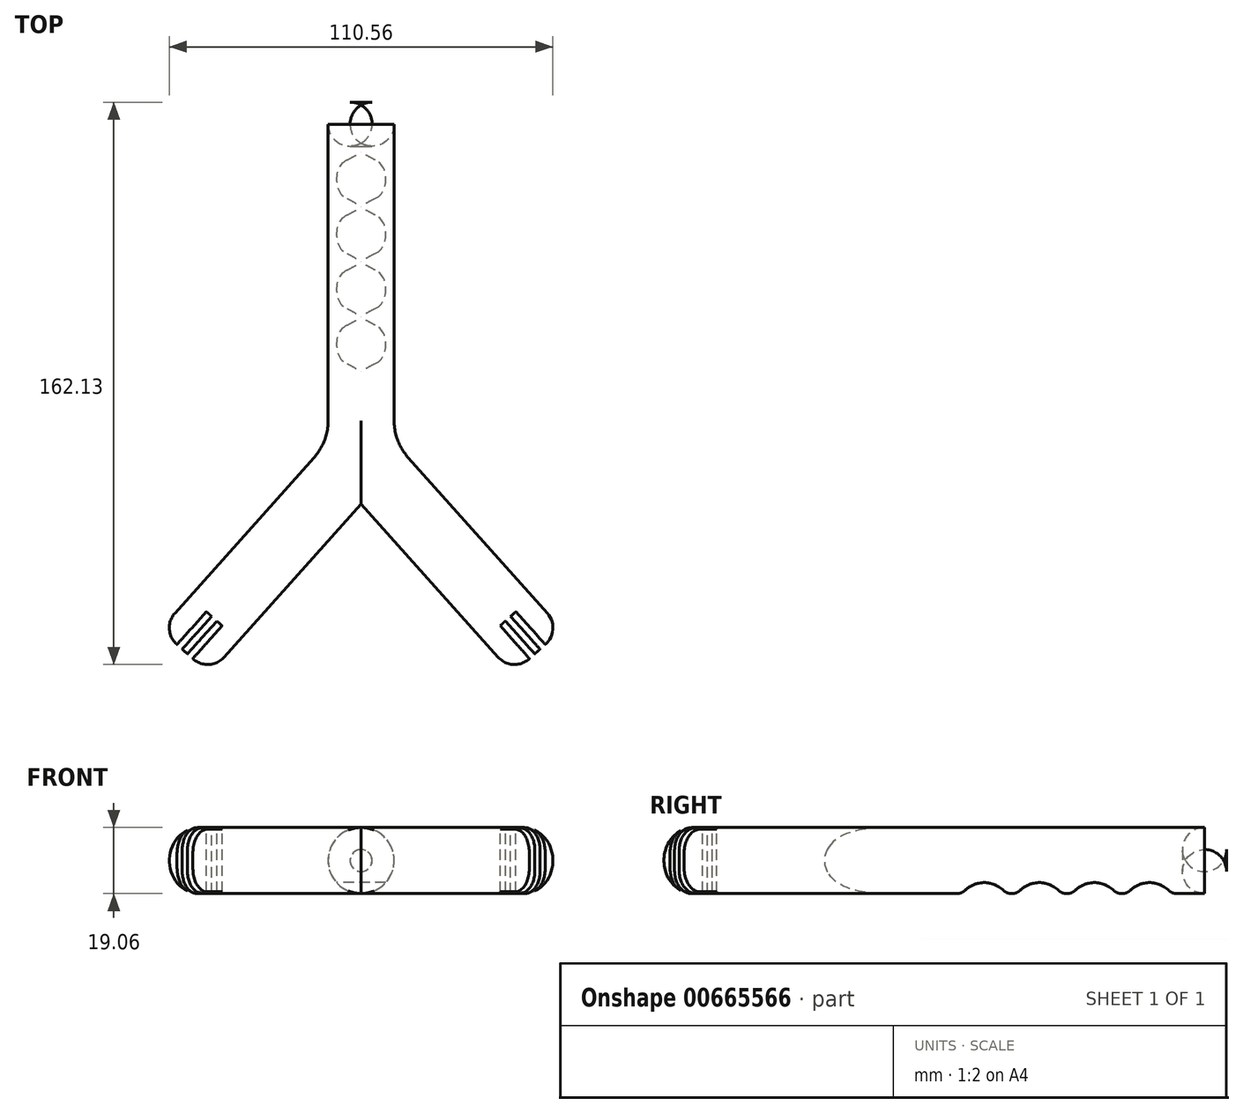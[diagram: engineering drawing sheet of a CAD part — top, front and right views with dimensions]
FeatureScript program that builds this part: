
annotation { "Feature Type Name" : "Feature", "Feature Type Description" : "" }
export const myFeature = defineFeature(function(context is Context, id is Id, definition is map)
    precondition{}
    {
        {
            var Q0;
            Q0=qCreatedBy(makeId("Front.planeOp"),FACE);
            var sketch = newSketch(context, id + "F0", { "sketchPlane" : qUnion([Q0])});
            skCircle(sketch, "E0", {"center": v(0, 0) * mm, "radius": 9.53 * mm});
            skSolve(sketch);
        }
        {
            var Q0;
            Q0=qCreatedBy(makeId("Top.planeOp"),FACE);
            var sketch = newSketch(context, id + "F1", { "sketchPlane" : qUnion([Q0])});
            skLineSegment(sketch, "E1", {"start": v(6.47, -108.83) * mm, "end": v(50.8, -158.4) * mm});
            skLineSegment(sketch, "E2", {"start": v(0, -91.9) * mm, "end": v(0, 0) * mm});
            skPoint(sketch, "E3.visualSharp", {"position": v(0, -101.6) * mm});
            skArc(sketch, "E3.filletArc", {"start": v(0, -91.9) * mm, "mid": v(1.67, -100.96) * mm, "end": v(6.47, -108.83) * mm});
            skSolve(sketch);
        }
        {
            var Q0;
            Q0=makeQuery(id+"F0.imprint","IMPRINT",FACE,{"disambiguationData":[TD([[makeQuery(id+"F0.imprint","IMPRINT",EDGE,{"derivedFrom":sQuery(id+"F0.wireOp",EDGE,"E0")}),1.0]])]});
            var Q1;
            Q1=sQuery(id+"F1.wireOp",EDGE,"E2");
            var Q2;
            Q2=sQuery(id+"F1.wireOp",EDGE,"E1");
            var Q3;
            Q3=sQuery(id+"F1.wireOp",EDGE,"3JrWUsI6-woq9-sjH6-vDIZ-4JQYBJ9BbOre");
            var Q4;
            Q4=sQuery(id+"F1.wireOp",EDGE,"61547c2f-0ffb-42c4-a759-9a06780f6b13.filletArc");
            var Q5;
            Q5=sQuery(id+"F1.wireOp",EDGE,"E3.filletArc");
            sweep(context, id + "F2", {"profiles" : qUnion([Q0]), "path" : qUnion([Q1, Q2, Q3, Q4, Q5])});
        }
        {
            var Q0;
            Q0=qCreatedBy(makeId("Top.planeOp"),FACE);
            var sketch = newSketch(context, id + "F3", { "sketchPlane" : qUnion([Q0])});
            skLineSegment(sketch, "E4", {"start": v(0, 0) * mm, "end": v(0, -91.9) * mm});
            skLineSegment(sketch, "E5", {"start": v(-6.47, -108.83) * mm, "end": v(-50.8, -158.4) * mm});
            skPoint(sketch, "E6.visualSharp", {"position": v(0, -101.6) * mm});
            skArc(sketch, "E6.filletArc", {"start": v(-6.47, -108.83) * mm, "mid": v(-1.67, -100.96) * mm, "end": v(0, -91.9) * mm});
            skSolve(sketch);
        }
        {
            var Q0;
            Q0=makeQuery(id+"F2.opSweep","CAP_FACE",FACE,{"disambiguationData":[OSD([sQuery(id+"F0.wireOp",EDGE,"E0"),sQuery(id+"F1.wireOp",VERTEX,"E2.end")])],"isStart":true});
            var Q1;
            Q1=sQuery(id+"F3.wireOp",EDGE,"E4");
            var Q2;
            Q2=sQuery(id+"F3.wireOp",EDGE,"E6.filletArc");
            var Q3;
            Q3=sQuery(id+"F3.wireOp",EDGE,"E5");
            sweep(context, id + "F4", {"operationType" : NewBodyOperationType.ADD, "profiles" : qUnion([Q0]), "path" : qUnion([Q1, Q2, Q3])});
        }
        {
            var Q0;
            Q0=makeQuery(id+"F2.opSweep","CAP_EDGE",EDGE,{"disambiguationData":[OSD([sQuery(id+"F0.wireOp",EDGE,"E0"),sQuery(id+"F1.wireOp",VERTEX,"E1.end")])],"isStart":false});
            var Q1;
            Q1=makeQuery(id+"F4.opSweep","CAP_EDGE",EDGE,{"disambiguationData":[OSD([sQuery(id+"F0.wireOp",EDGE,"E0"),sQuery(id+"F1.wireOp",VERTEX,"E2.end"),sQuery(id+"F3.wireOp",VERTEX,"E5.end")])],"isStart":false});
            var Q2;
            Q2=makeQuery(id+"F2.opSweep","CAP_EDGE",EDGE,{"disambiguationData":[OSD([sQuery(id+"F0.wireOp",EDGE,"E0"),sQuery(id+"F1.wireOp",VERTEX,"E2.end")])],"isStart":true});
            fillet(context, id + "F5", {"entities" : qUnion([Q0, Q1, Q2]), "radius" : 6.35 * mm, "tangentPropagation" : true, "allowEdgeOverflow" : false});
        }
        {
            var Q0;
            Q0=qCreatedBy(makeId("Top.planeOp"),FACE);
            var sketch = newSketch(context, id + "F6", { "sketchPlane" : qUnion([Q0])});
            skLineSegment(sketch, "E7", {"start": v(48.53, -160.43) * mm, "end": v(40.06, -150.96) * mm});
            skLineSegment(sketch, "E8", {"start": v(40.06, -150.96) * mm, "end": v(41.58, -149.6) * mm});
            skLineSegment(sketch, "E9", {"start": v(41.58, -149.6) * mm, "end": v(50.04, -159.07) * mm});
            skLineSegment(sketch, "E10", {"start": v(50.04, -159.07) * mm, "end": v(48.53, -160.43) * mm});
            skLineSegment(sketch, "E11", {"start": v(50.8, -158.4) * mm, "end": v(45.21, -152.15) * mm, "construction": true});
            skLineSegment(sketch, "E12.MirrorCS", {"start": v(44.6, -146.9) * mm, "end": v(43.1, -148.25) * mm});
            skLineSegment(sketch, "E13.MirrorCS", {"start": v(53.07, -156.36) * mm, "end": v(44.6, -146.9) * mm});
            skLineSegment(sketch, "E14.MirrorCS", {"start": v(51.56, -157.72) * mm, "end": v(53.07, -156.36) * mm});
            skLineSegment(sketch, "E15.MirrorCS", {"start": v(43.1, -148.25) * mm, "end": v(51.56, -157.72) * mm});
            skLineSegment(sketch, "E16", {"start": v(0, 0) * mm, "end": v(0, -157.78) * mm, "construction": true});
            skLineSegment(sketch, "E17.MirrorCS", {"start": v(-50.04, -159.07) * mm, "end": v(-48.53, -160.43) * mm});
            skLineSegment(sketch, "E18.MirrorCS", {"start": v(-51.56, -157.72) * mm, "end": v(-53.07, -156.36) * mm});
            skLineSegment(sketch, "E19.MirrorCS", {"start": v(-40.06, -150.96) * mm, "end": v(-41.58, -149.6) * mm});
            skLineSegment(sketch, "E20.MirrorCS", {"start": v(-44.6, -146.9) * mm, "end": v(-43.1, -148.25) * mm});
            skLineSegment(sketch, "E21.MirrorCS", {"start": v(-41.58, -149.6) * mm, "end": v(-50.04, -159.07) * mm});
            skLineSegment(sketch, "E22.MirrorCS", {"start": v(-50.8, -158.4) * mm, "end": v(-45.21, -152.15) * mm, "construction": true});
            skLineSegment(sketch, "E23.MirrorCS", {"start": v(-48.53, -160.43) * mm, "end": v(-40.06, -150.96) * mm});
            skLineSegment(sketch, "E24.MirrorCS", {"start": v(-43.1, -148.25) * mm, "end": v(-51.56, -157.72) * mm});
            skLineSegment(sketch, "E25.MirrorCS", {"start": v(-53.07, -156.36) * mm, "end": v(-44.6, -146.9) * mm});
            skSolve(sketch);
        }
        {
            var Q0;
            Q0 = qSketchRegion(id + "F6", true);
            extrude(context, id + "F7", {"entities" : qUnion([Q0]), "operationType" : NewBodyOperationType.REMOVE, "endBound" : BoundingType.THROUGH_ALL, "oppositeDirection" : true, "depth" : 25.4 * mm, "offsetDistance" : 25.4 * mm, "hasSecondDirection" : true, "secondDirectionBound" : SecondDirectionBoundingType.THROUGH_ALL, "secondDirectionOppositeDirection" : false, "secondDirectionDepth" : 25.4 * mm});
        }
        {
            var Q0;
            Q0=qCreatedBy(makeId("Right.planeOp"),FACE);
            var sketch = newSketch(context, id + "F8", { "sketchPlane" : qUnion([Q0])});
            skLineSegment(sketch, "E26", {"start": v(-6.35, -9.52) * mm, "end": v(-14.45, -9.52) * mm, "construction": true});
            skLineSegment(sketch, "E27.0", {"start": v(-6.35, -9.53) * mm, "end": v(-6.35, 9.53) * mm, "construction": true});
            skArc(sketch, "E28", {"start": v(-16.67, -8.62) * mm, "mid": v(-22.22, -6.35) * mm, "end": v(-27.78, -8.62) * mm});
            skArc(sketch, "E29", {"start": v(-32.54, -8.62) * mm, "mid": v(-38.1, -6.35) * mm, "end": v(-43.66, -8.62) * mm});
            skArc(sketch, "E30", {"start": v(-48.42, -8.62) * mm, "mid": v(-53.98, -6.35) * mm, "end": v(-59.53, -8.62) * mm});
            skArc(sketch, "E31", {"start": v(-64.3, -8.62) * mm, "mid": v(-69.85, -6.35) * mm, "end": v(-75.4, -8.62) * mm});
            skLineSegment(sketch, "E32", {"start": v(-30, -9.52) * mm, "end": v(-30.32, -9.52) * mm});
            skLineSegment(sketch, "E33", {"start": v(-46.2, -9.52) * mm, "end": v(-45.88, -9.52) * mm});
            skLineSegment(sketch, "E34", {"start": v(-62.07, -9.52) * mm, "end": v(-61.75, -9.52) * mm});
            skLineSegment(sketch, "E35", {"start": v(-15.88, -9.52) * mm, "end": v(-28.58, -9.52) * mm, "construction": true});
            skLineSegment(sketch, "E36", {"start": v(-31.75, -9.52) * mm, "end": v(-44.45, -9.52) * mm, "construction": true});
            skLineSegment(sketch, "E37", {"start": v(-47.62, -9.52) * mm, "end": v(-60.33, -9.52) * mm, "construction": true});
            skLineSegment(sketch, "E38", {"start": v(-63.5, -9.52) * mm, "end": v(-76.2, -9.52) * mm, "construction": true});
            skLineSegment(sketch, "E39", {"start": v(-46.04, -9.52) * mm, "end": v(-46.04, -8.23) * mm, "construction": true});
            skLineSegment(sketch, "E40", {"start": v(-69.85, -6.35) * mm, "end": v(-22.23, -6.35) * mm, "construction": true});
            skPoint(sketch, "E41.newPointA", {"position": v(-15.88, -9.53) * mm});
            skPoint(sketch, "E41.newPointB", {"position": v(-85.72, -9.52) * mm});
            skArc(sketch, "E41.filletArc", {"start": v(-16.67, -8.62) * mm, "mid": v(-15.65, -9.29) * mm, "end": v(-14.45, -9.52) * mm});
            skPoint(sketch, "E42.visualSharp", {"position": v(-28.58, -9.53) * mm});
            skArc(sketch, "E42.filletArc", {"start": v(-30, -9.52) * mm, "mid": v(-28.8, -9.29) * mm, "end": v(-27.78, -8.62) * mm});
            skPoint(sketch, "E43.visualSharp", {"position": v(-31.75, -9.52) * mm});
            skArc(sketch, "E43.filletArc", {"start": v(-32.54, -8.62) * mm, "mid": v(-31.52, -9.29) * mm, "end": v(-30.32, -9.52) * mm});
            skPoint(sketch, "E44.visualSharp", {"position": v(-44.45, -9.52) * mm});
            skArc(sketch, "E44.filletArc", {"start": v(-45.88, -9.52) * mm, "mid": v(-44.68, -9.29) * mm, "end": v(-43.66, -8.62) * mm});
            skPoint(sketch, "E45.visualSharp", {"position": v(-47.62, -9.52) * mm});
            skArc(sketch, "E45.filletArc", {"start": v(-48.42, -8.62) * mm, "mid": v(-47.4, -9.29) * mm, "end": v(-46.2, -9.52) * mm});
            skPoint(sketch, "E46.visualSharp", {"position": v(-60.33, -9.52) * mm});
            skArc(sketch, "E46.filletArc", {"start": v(-61.75, -9.52) * mm, "mid": v(-60.55, -9.29) * mm, "end": v(-59.53, -8.62) * mm});
            skPoint(sketch, "E47.visualSharp", {"position": v(-63.5, -9.52) * mm});
            skArc(sketch, "E47.filletArc", {"start": v(-64.3, -8.62) * mm, "mid": v(-63.27, -9.29) * mm, "end": v(-62.07, -9.52) * mm});
            skLineSegment(sketch, "E48", {"start": v(-77.63, -9.53) * mm, "end": v(-78.14, -9.53) * mm, "construction": true});
            skPoint(sketch, "E49.visualSharp", {"position": v(-76.2, -9.53) * mm});
            skArc(sketch, "E49.filletArc", {"start": v(-77.63, -9.53) * mm, "mid": v(-76.43, -9.29) * mm, "end": v(-75.4, -8.62) * mm});
            skLineSegment(sketch, "E50", {"start": v(-14.45, -9.52) * mm, "end": v(-14.45, -12.25) * mm});
            skLineSegment(sketch, "E51", {"start": v(-14.45, -12.25) * mm, "end": v(-77.63, -12.25) * mm});
            skLineSegment(sketch, "E52", {"start": v(-77.63, -12.25) * mm, "end": v(-77.63, -9.53) * mm});
            skSolve(sketch);
        }
        {
            var Q0;
            Q0 = qSketchRegion(id + "F8", true);
            extrude(context, id + "F9", {"entities" : qUnion([Q0]), "operationType" : NewBodyOperationType.REMOVE, "endBound" : BoundingType.THROUGH_ALL, "depth" : 25.4 * mm, "offsetDistance" : 25.4 * mm, "hasSecondDirection" : true, "secondDirectionBound" : SecondDirectionBoundingType.THROUGH_ALL, "secondDirectionOppositeDirection" : true, "secondDirectionDepth" : 25.4 * mm});
        }
    });
